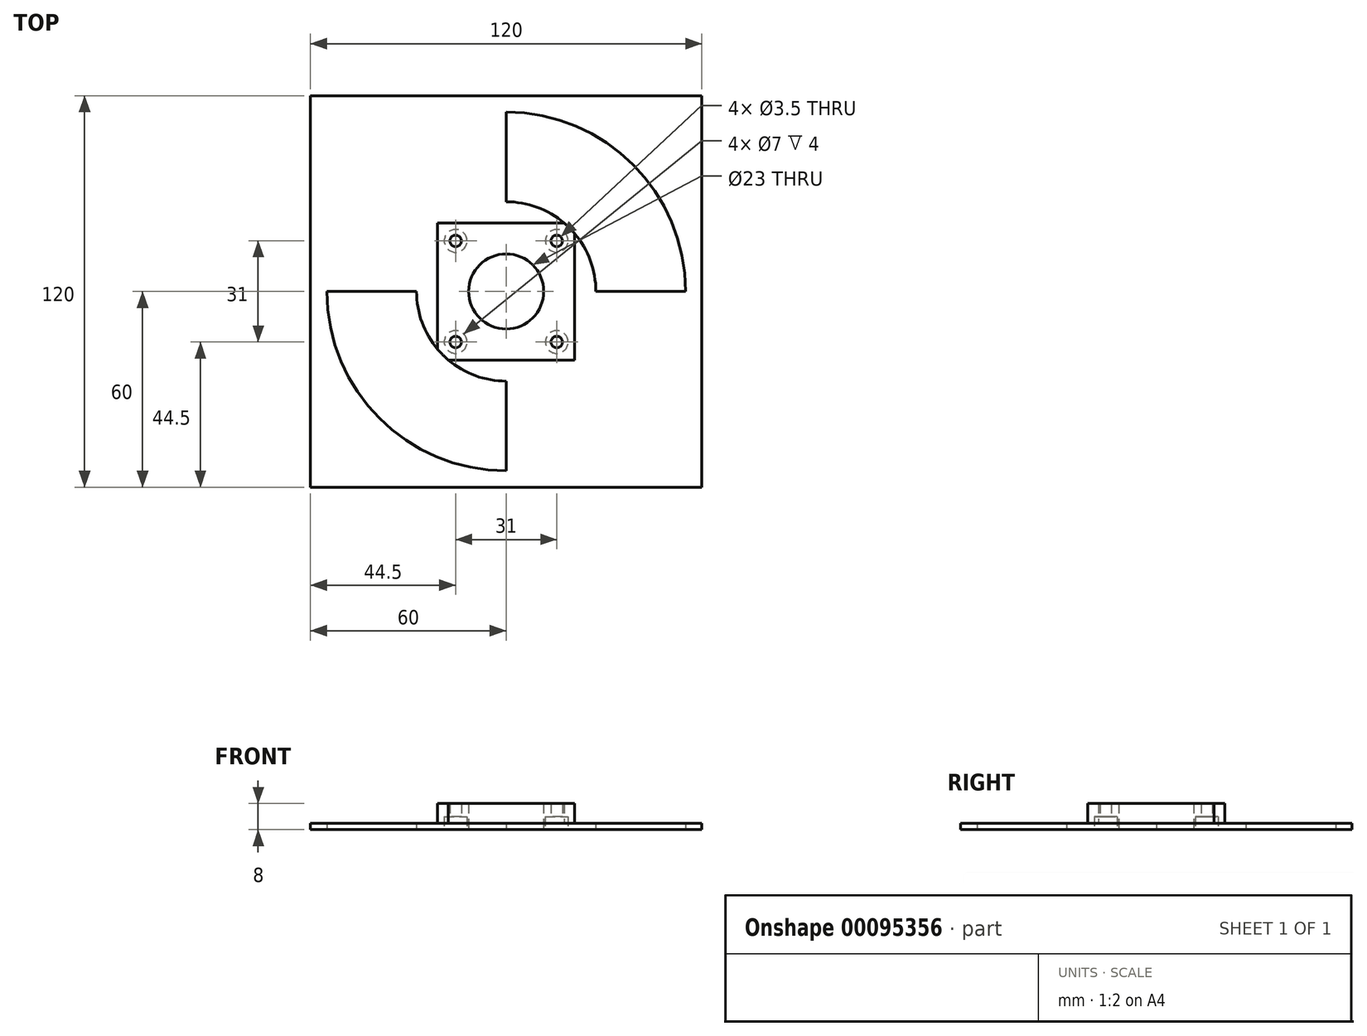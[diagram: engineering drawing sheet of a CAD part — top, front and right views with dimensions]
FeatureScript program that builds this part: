
annotation { "Feature Type Name" : "Feature", "Feature Type Description" : "" }
export const myFeature = defineFeature(function(context is Context, id is Id, definition is map)
    precondition{}
    {
        {
            var Q0;
            Q0=qCreatedBy(makeId("Top.planeOp"),FACE);
            var sketch = newSketch(context, id + "F0", { "sketchPlane" : qUnion([Q0])});
            skCircle(sketch, "E0", {"center": v(0, 0) * mm, "radius": 11.5 * mm});
            skLineSegment(sketch, "E1.bottom", {"start": v(21, 21) * mm, "end": v(-21, 21) * mm});
            skLineSegment(sketch, "E1.top", {"start": v(21, -21) * mm, "end": v(-21, -21) * mm});
            skLineSegment(sketch, "E1.left", {"start": v(21, 21) * mm, "end": v(21, -21) * mm});
            skLineSegment(sketch, "E1.right", {"start": v(-21, 21) * mm, "end": v(-21, -21) * mm});
            skCircle(sketch, "E2", {"center": v(15.5, 15.5) * mm, "radius": 1.75 * mm});
            skCircle(sketch, "E3", {"center": v(-15.5, 15.5) * mm, "radius": 1.75 * mm});
            skCircle(sketch, "E4", {"center": v(-15.5, -15.5) * mm, "radius": 1.75 * mm});
            skCircle(sketch, "E5", {"center": v(15.5, -15.5) * mm, "radius": 1.75 * mm});
            skLineSegment(sketch, "E6.bottom", {"start": v(60, 60) * mm, "end": v(-60, 60) * mm});
            skLineSegment(sketch, "E6.top", {"start": v(60, -60) * mm, "end": v(-60, -60) * mm});
            skLineSegment(sketch, "E6.left", {"start": v(60, 60) * mm, "end": v(60, -60) * mm});
            skLineSegment(sketch, "E6.right", {"start": v(-60, 60) * mm, "end": v(-60, -60) * mm});
            skSolve(sketch);
        }
        {
            var Q0;
            Q0=makeQuery(id+"F0.imprint","IMPRINT",FACE,{"disambiguationData":[TD([[makeQuery(id+"F0.imprint","IMPRINT",EDGE,{"derivedFrom":sQuery(id+"F0.wireOp",EDGE,"E0")}),-1.0]])]});
            extrude(context, id + "F1", {"entities" : qUnion([Q0]), "depth" : 5 * mm});
        }
        {
            var Q0;
            Q0 = qSketchRegion(id + "F0", true);
            extrude(context, id + "F2", {"entities" : qUnion([Q0]), "operationType" : NewBodyOperationType.ADD, "depth" : 2 * mm});
        }
        {
            var Q0;
            {var subQ0=sQuery(id+"F0.wireOp",EDGE,"E1.right");var subQ1=sQuery(id+"F0.wireOp",EDGE,"E1.left");var subQ2=sQuery(id+"F0.wireOp",EDGE,"E1.top");var subQ3=sQuery(id+"F0.wireOp",EDGE,"E1.bottom");Q0=makeQuery(id+"F2.boolean.opBoolean","MERGE",FACE,{"derivedFrom":[makeQuery(id+"F1.opExtrude","CAP_FACE",FACE,{"disambiguationData":[OSD([sQuery(id+"F0.wireOp",EDGE,"E0"),subQ3,subQ2,subQ1,subQ0,sQuery(id+"F0.wireOp",EDGE,"E2"),sQuery(id+"F0.wireOp",EDGE,"E3"),sQuery(id+"F0.wireOp",EDGE,"E4"),sQuery(id+"F0.wireOp",EDGE,"E5")])],"isStart":true}),makeQuery(id+"F2.opExtrude","CAP_FACE",FACE,{"disambiguationData":[OSD([subQ3,subQ2,subQ1,subQ0,sQuery(id+"F0.wireOp",EDGE,"E6.bottom"),sQuery(id+"F0.wireOp",EDGE,"E6.top"),sQuery(id+"F0.wireOp",EDGE,"E6.left"),sQuery(id+"F0.wireOp",EDGE,"E6.right")])],"isStart":true})]});}
            var sketch = newSketch(context, id + "F3", { "sketchPlane" : qUnion([Q0])});
            skCircle(sketch, "E7", {"center": v(0, 0) * mm, "radius": 55 * mm});
            skCircle(sketch, "E8", {"center": v(0, 0) * mm, "radius": 27.5 * mm});
            skLineSegment(sketch, "E9", {"start": v(0, 55) * mm, "end": v(0, 27.5) * mm});
            skLineSegment(sketch, "E10", {"start": v(-27.5, 0) * mm, "end": v(-55, 0) * mm});
            skSolve(sketch);
        }
        {
            var Q0;
            {var subQ0=sQuery(id+"F3.wireOp",EDGE,"E9");Q0=makeQuery(id+"F3.imprint","IMPRINT",FACE,{"disambiguationData":[TD([[makeQuery(id+"F3.imprint","IMPRINT",EDGE,{"derivedFrom":subQ0}),-1.0]])]});}
            extrude(context, id + "F4", {"entities" : qUnion([Q0]), "operationType" : NewBodyOperationType.REMOVE, "oppositeDirection" : true, "depth" : 2 * mm});
        }
        {
            var Q0;
            Q0=makeQuery(id+"F4.boolean.opBoolean","COPY",FACE,{"derivedFrom":makeQuery(id+"F4.opExtrude","CAP_FACE",FACE,{"disambiguationData":[OSD([sQuery(id+"F3.wireOp",EDGE,"E7"),sQuery(id+"F3.wireOp",EDGE,"E8"),sQuery(id+"F3.wireOp",EDGE,"E9"),sQuery(id+"F3.wireOp",EDGE,"E10")])],"isStart":false})});
            extrude(context, id + "F5", {"entities" : qUnion([Q0]), "operationType" : NewBodyOperationType.REMOVE, "oppositeDirection" : true, "depth" : 3 * mm});
        }
        {
            var Q0;
            {var subQ0=sQuery(id+"F0.wireOp",EDGE,"E1.right");var subQ1=sQuery(id+"F0.wireOp",EDGE,"E1.left");var subQ2=sQuery(id+"F0.wireOp",EDGE,"E1.top");var subQ3=sQuery(id+"F0.wireOp",EDGE,"E1.bottom");Q0=makeQuery(id+"F2.boolean.opBoolean","MERGE",FACE,{"derivedFrom":[makeQuery(id+"F1.opExtrude","CAP_FACE",FACE,{"disambiguationData":[OSD([sQuery(id+"F0.wireOp",EDGE,"E0"),subQ3,subQ2,subQ1,subQ0,sQuery(id+"F0.wireOp",EDGE,"E2"),sQuery(id+"F0.wireOp",EDGE,"E3"),sQuery(id+"F0.wireOp",EDGE,"E4"),sQuery(id+"F0.wireOp",EDGE,"E5")])],"isStart":true}),makeQuery(id+"F2.opExtrude","CAP_FACE",FACE,{"disambiguationData":[OSD([subQ3,subQ2,subQ1,subQ0,sQuery(id+"F0.wireOp",EDGE,"E6.bottom"),sQuery(id+"F0.wireOp",EDGE,"E6.top"),sQuery(id+"F0.wireOp",EDGE,"E6.left"),sQuery(id+"F0.wireOp",EDGE,"E6.right")])],"isStart":true})]});}
            var sketch = newSketch(context, id + "F6", { "sketchPlane" : qUnion([Q0])});
            skCircle(sketch, "E11", {"center": v(15.5, 15.5) * mm, "radius": 3.5 * mm});
            skCircle(sketch, "E12", {"center": v(-15.5, 15.5) * mm, "radius": 3.5 * mm});
            skCircle(sketch, "E13", {"center": v(-15.5, -15.5) * mm, "radius": 3.5 * mm});
            skCircle(sketch, "E14", {"center": v(15.5, -15.5) * mm, "radius": 3.5 * mm});
            skSolve(sketch);
        }
        {
            var Q0;
            Q0=makeQuery(id+"F6.imprint","IMPRINT",FACE,{"disambiguationData":[TD([[makeQuery(id+"F6.imprint","IMPRINT",EDGE,{"derivedFrom":sQuery(id+"F6.wireOp",EDGE,"E12")}),1.0]])]});
            extrude(context, id + "F7", {"entities" : qUnion([Q0]), "operationType" : NewBodyOperationType.REMOVE, "oppositeDirection" : true, "depth" : 4 * mm});
        }
        {
            var Q0;
            {var subQ0=sQuery(id+"F0.wireOp",EDGE,"E1.right");var subQ1=sQuery(id+"F0.wireOp",EDGE,"E1.left");var subQ2=sQuery(id+"F0.wireOp",EDGE,"E1.top");var subQ3=sQuery(id+"F0.wireOp",EDGE,"E1.bottom");Q0=makeQuery(id+"F2.boolean.opBoolean","MERGE",FACE,{"derivedFrom":[makeQuery(id+"F1.opExtrude","CAP_FACE",FACE,{"disambiguationData":[OSD([sQuery(id+"F0.wireOp",EDGE,"E0"),subQ3,subQ2,subQ1,subQ0,sQuery(id+"F0.wireOp",EDGE,"E2"),sQuery(id+"F0.wireOp",EDGE,"E3"),sQuery(id+"F0.wireOp",EDGE,"E4"),sQuery(id+"F0.wireOp",EDGE,"E5")])],"isStart":true}),makeQuery(id+"F2.opExtrude","CAP_FACE",FACE,{"disambiguationData":[OSD([subQ3,subQ2,subQ1,subQ0,sQuery(id+"F0.wireOp",EDGE,"E6.bottom"),sQuery(id+"F0.wireOp",EDGE,"E6.top"),sQuery(id+"F0.wireOp",EDGE,"E6.left"),sQuery(id+"F0.wireOp",EDGE,"E6.right")])],"isStart":true})]});}
            var sketch = newSketch(context, id + "F8", { "sketchPlane" : qUnion([Q0])});
            skCircle(sketch, "E15", {"center": v(15.5, 15.5) * mm, "radius": 3.5 * mm});
            skSolve(sketch);
        }
        {
            var Q0;
            Q0=makeQuery(id+"F8.imprint","IMPRINT",FACE,{"disambiguationData":[TD([[makeQuery(id+"F8.imprint","IMPRINT",EDGE,{"derivedFrom":sQuery(id+"F8.wireOp",EDGE,"E15")}),1.0]])]});
            extrude(context, id + "F9", {"entities" : qUnion([Q0]), "operationType" : NewBodyOperationType.REMOVE, "oppositeDirection" : true, "depth" : 4 * mm});
        }
        {
            var Q0;
            {var subQ0=sQuery(id+"F0.wireOp",EDGE,"E1.right");var subQ1=sQuery(id+"F0.wireOp",EDGE,"E1.left");var subQ2=sQuery(id+"F0.wireOp",EDGE,"E1.top");var subQ3=sQuery(id+"F0.wireOp",EDGE,"E1.bottom");Q0=makeQuery(id+"F2.boolean.opBoolean","MERGE",FACE,{"derivedFrom":[makeQuery(id+"F1.opExtrude","CAP_FACE",FACE,{"disambiguationData":[OSD([sQuery(id+"F0.wireOp",EDGE,"E0"),subQ3,subQ2,subQ1,subQ0,sQuery(id+"F0.wireOp",EDGE,"E2"),sQuery(id+"F0.wireOp",EDGE,"E3"),sQuery(id+"F0.wireOp",EDGE,"E4"),sQuery(id+"F0.wireOp",EDGE,"E5")])],"isStart":true}),makeQuery(id+"F2.opExtrude","CAP_FACE",FACE,{"disambiguationData":[OSD([subQ3,subQ2,subQ1,subQ0,sQuery(id+"F0.wireOp",EDGE,"E6.bottom"),sQuery(id+"F0.wireOp",EDGE,"E6.top"),sQuery(id+"F0.wireOp",EDGE,"E6.left"),sQuery(id+"F0.wireOp",EDGE,"E6.right")])],"isStart":true})]});}
            var sketch = newSketch(context, id + "F10", { "sketchPlane" : qUnion([Q0])});
            skCircle(sketch, "E16", {"center": v(-15.5, -15.5) * mm, "radius": 3.5 * mm});
            skCircle(sketch, "E17", {"center": v(15.5, -15.5) * mm, "radius": 3.5 * mm});
            skSolve(sketch);
        }
        {
            var Q0;
            Q0=makeQuery(id+"F10.imprint","IMPRINT",FACE,{"disambiguationData":[TD([[makeQuery(id+"F10.imprint","IMPRINT",EDGE,{"derivedFrom":sQuery(id+"F10.wireOp",EDGE,"E16")}),1.0]])]});
            var Q1;
            Q1=makeQuery(id+"F10.imprint","IMPRINT",FACE,{"disambiguationData":[TD([[makeQuery(id+"F10.imprint","IMPRINT",EDGE,{"derivedFrom":sQuery(id+"F10.wireOp",EDGE,"E17")}),1.0]])]});
            var Q2;
            Q2=sQuery(id+"F10.wireOp",EDGE,"E16");
            var Q3;
            Q3=sQuery(id+"F10.wireOp",EDGE,"E17");
            extrude(context, id + "F11", {"entities" : qUnion([Q0, Q1]), "operationType" : NewBodyOperationType.REMOVE, "surfaceEntities" : qUnion([Q2, Q3]), "oppositeDirection" : true, "depth" : 4 * mm});
        }
        {
            var Q0;
            Q0=makeQuery(id+"F1.opExtrude","CAP_FACE",FACE,{"disambiguationData":[OSD([sQuery(id+"F0.wireOp",EDGE,"E0"),sQuery(id+"F0.wireOp",EDGE,"E1.bottom"),sQuery(id+"F0.wireOp",EDGE,"E1.top"),sQuery(id+"F0.wireOp",EDGE,"E1.left"),sQuery(id+"F0.wireOp",EDGE,"E1.right"),sQuery(id+"F0.wireOp",EDGE,"E2"),sQuery(id+"F0.wireOp",EDGE,"E3"),sQuery(id+"F0.wireOp",EDGE,"E4"),sQuery(id+"F0.wireOp",EDGE,"E5")])],"isStart":false});
            extrude(context, id + "F12", {"entities" : qUnion([Q0]), "operationType" : NewBodyOperationType.ADD, "depth" : 3 * mm});
        }
        {
            var Q0;
            {var subQ0=sQuery(id+"F0.wireOp",EDGE,"E1.right");var subQ1=sQuery(id+"F0.wireOp",EDGE,"E1.left");var subQ2=sQuery(id+"F0.wireOp",EDGE,"E1.top");var subQ3=sQuery(id+"F0.wireOp",EDGE,"E1.bottom");Q0=makeQuery(id+"F2.boolean.opBoolean","MERGE",FACE,{"derivedFrom":[makeQuery(id+"F1.opExtrude","CAP_FACE",FACE,{"disambiguationData":[OSD([sQuery(id+"F0.wireOp",EDGE,"E0"),subQ3,subQ2,subQ1,subQ0,sQuery(id+"F0.wireOp",EDGE,"E2"),sQuery(id+"F0.wireOp",EDGE,"E3"),sQuery(id+"F0.wireOp",EDGE,"E4"),sQuery(id+"F0.wireOp",EDGE,"E5")])],"isStart":true}),makeQuery(id+"F2.opExtrude","CAP_FACE",FACE,{"disambiguationData":[OSD([subQ3,subQ2,subQ1,subQ0,sQuery(id+"F0.wireOp",EDGE,"E6.bottom"),sQuery(id+"F0.wireOp",EDGE,"E6.top"),sQuery(id+"F0.wireOp",EDGE,"E6.left"),sQuery(id+"F0.wireOp",EDGE,"E6.right")])],"isStart":true})]});}
            var sketch = newSketch(context, id + "F13", { "sketchPlane" : qUnion([Q0])});
            skCircle(sketch, "E18", {"center": v(0, 0) * mm, "radius": 55 * mm});
            skCircle(sketch, "E19", {"center": v(0, 0) * mm, "radius": 27.5 * mm});
            skLineSegment(sketch, "E20", {"start": v(0, -27.5) * mm, "end": v(0, -55) * mm});
            skLineSegment(sketch, "E21", {"start": v(27.5, 0) * mm, "end": v(55, 0) * mm});
            skSolve(sketch);
        }
        {
            var Q0;
            {var subQ0=sQuery(id+"F13.wireOp",EDGE,"E20");Q0=makeQuery(id+"F13.imprint","IMPRINT",FACE,{"disambiguationData":[TD([[makeQuery(id+"F13.imprint","IMPRINT",EDGE,{"derivedFrom":subQ0}),1.0]])]});}
            extrude(context, id + "F14", {"entities" : qUnion([Q0]), "operationType" : NewBodyOperationType.REMOVE, "oppositeDirection" : true, "depth" : 2 * mm});
        }
        {
            var Q0;
            Q0=makeQuery(id+"F14.boolean.opBoolean","COPY",FACE,{"derivedFrom":makeQuery(id+"F14.opExtrude","CAP_FACE",FACE,{"disambiguationData":[OSD([sQuery(id+"F13.wireOp",EDGE,"E18"),sQuery(id+"F13.wireOp",EDGE,"E19"),sQuery(id+"F13.wireOp",EDGE,"E20"),sQuery(id+"F13.wireOp",EDGE,"E21")])],"isStart":false})});
            extrude(context, id + "F15", {"entities" : qUnion([Q0]), "operationType" : NewBodyOperationType.REMOVE, "oppositeDirection" : true, "depth" : 8 * mm});
        }
    });
